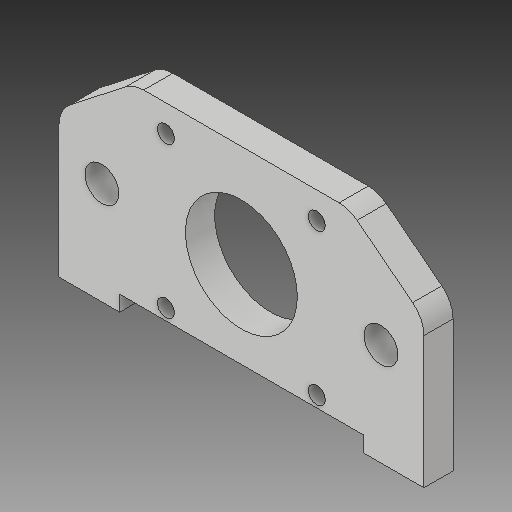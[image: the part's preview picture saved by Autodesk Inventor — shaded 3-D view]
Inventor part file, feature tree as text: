
AUTODESK INVENTOR PART (.ipt)
format: ipt  version: 2019 (Build 230136000, 136)  size: 158,208 bytes
history: native  units: mm
features: extrude x1, fillet x1, sketch x1
ambient origin geometry x8: Origin, YZ Plane, XZ Plane, XY Plane, X Axis, Y Axis, Z Axis, Center Point
bodies: Body1 (feature_tree)
feature tree (3):
  extrude  "Extrusion2"  Depth=42.0mm
  fillet  "Fillet2"  Radius=22.340214mm
  sketch  "Sketch1"  dims[d0=30.0mm d1=30.0mm d3=22.340214mm d4=75.0mm d5=7.0mm d7=7.0mm d9=28.678mm d10=28.678mm d13=3.5mm d14=3.5mm d15=15.5mm d16=15.5mm d21=3.5mm d22=3.5mm d23=31.0mm d24=23.0mm d25=6.0mm d26=0.0mm d27=6.0mm d28=50.0mm d29=12.5mm d30=3.2mm d31=17.8mm d32=2.3mm d33=22.340214mm d34=44.281401mm d35=12.0mm d36=12.0mm d37=42.0mm]
